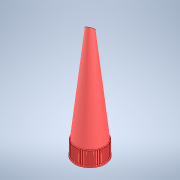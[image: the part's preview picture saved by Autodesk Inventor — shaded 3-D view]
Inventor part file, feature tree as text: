
AUTODESK INVENTOR PART (.ipt)
format: ipt  version: 2021 (Build 250183000, 183)  size: 1,020,416 bytes
history: mixed  units: in
note: dims shown in document units (in); Inventor stores cm internally (conversion verified against a paired STEP export)
features: sketch x3, plane x2, extrude x2, revolve x1, other x1, imported_body x1
ambient origin geometry x8: Origin, YZ Plane, XZ Plane, XY Plane, X Axis, Y Axis, Z Axis, Center Point
bodies: Solid1 (imported_parasolid)
feature tree (10):
  revolve  "Revolution2"  Angle=360.0deg
  plane  "Work Plane4"
  extrude  "Extrusion1"  Depth=0.3937in TaperAngle=0.0deg
  extrude  "Extrusion2"  TaperAngle=0.0deg  [1 undecoded]
  sketch  "Sketch2"  dims[d4=0.125in d5=360.0deg]
  plane  "Work Plane3"
  sketch  "Sketch3"  dims[d8=45.0deg d9=2.9921in d10=0.3937in d11=0.0in]
  sketch  "Sketch4"  dims[d12=0.7874in d13=0.0in d14=0.0in]
  other  "RipetizioneCircolare3"
  imported_body  NMx_Import_Brep_tag  [imported B-rep: ~7 faces, bbox_mm=[0.0, 0.0, 0.0]]
note: 1 required parameter value undecoded (feature->parameter linkage not recoverable at this tier; creation-order binding heuristic only, values carry confidence <= 0.55)
